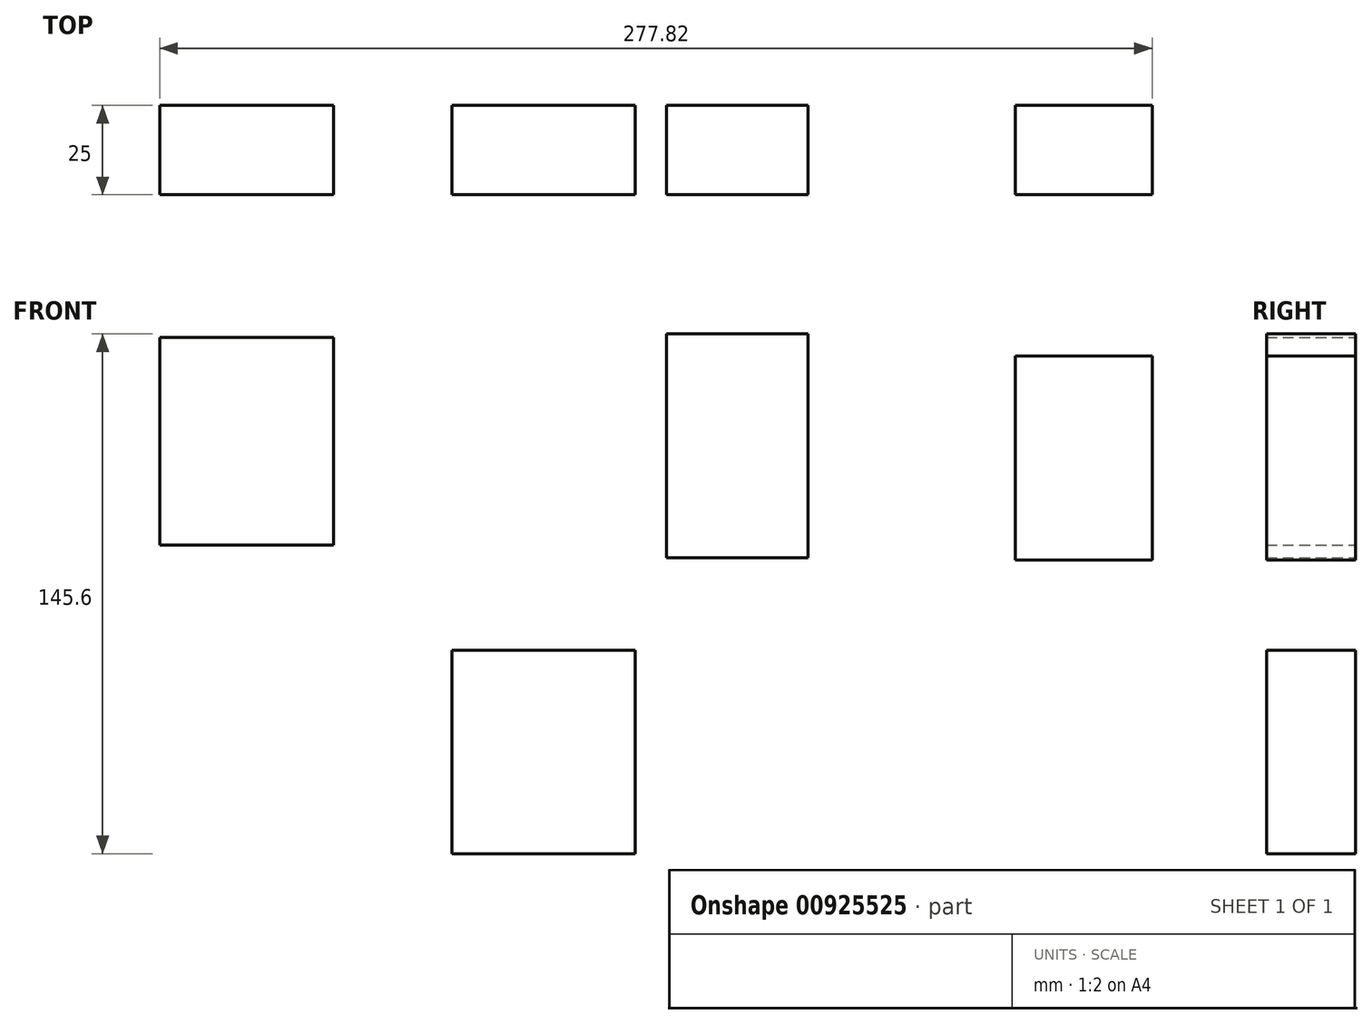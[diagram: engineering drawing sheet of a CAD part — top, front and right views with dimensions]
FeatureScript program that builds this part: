
annotation { "Feature Type Name" : "Feature", "Feature Type Description" : "" }
export const myFeature = defineFeature(function(context is Context, id is Id, definition is map)
    precondition{}
    {
        {
            var Q0;
            Q0=qCreatedBy(makeId("Front.planeOp"),FACE);
            var sketch = newSketch(context, id + "F0", { "sketchPlane" : qUnion([Q0])});
            skLineSegment(sketch, "E0.bottom", {"start": v(-145.24, 17.95) * mm, "end": v(-96.56, 17.95) * mm});
            skLineSegment(sketch, "E0.top", {"start": v(-145.24, 76.15) * mm, "end": v(-96.56, 76.15) * mm});
            skLineSegment(sketch, "E0.left", {"start": v(-145.24, 17.95) * mm, "end": v(-145.24, 76.15) * mm});
            skLineSegment(sketch, "E0.right", {"start": v(-96.56, 17.95) * mm, "end": v(-96.56, 76.15) * mm});
            skPoint(sketch, "E0.middle", {"position": v(-120.9, 47.05) * mm});
            skLineSegment(sketch, "E1.bottom", {"start": v(-3.4, 14.43) * mm, "end": v(36.19, 14.43) * mm});
            skLineSegment(sketch, "E1.top", {"start": v(-3.4, 77.14) * mm, "end": v(36.19, 77.14) * mm});
            skLineSegment(sketch, "E1.left", {"start": v(-3.4, 14.43) * mm, "end": v(-3.4, 77.14) * mm});
            skLineSegment(sketch, "E1.right", {"start": v(36.19, 14.43) * mm, "end": v(36.19, 77.14) * mm});
            skPoint(sketch, "E1.middle", {"position": v(16.4, 45.79) * mm});
            skLineSegment(sketch, "E2.bottom", {"start": v(94.28, 13.75) * mm, "end": v(132.58, 13.75) * mm});
            skLineSegment(sketch, "E2.top", {"start": v(94.28, 70.9) * mm, "end": v(132.58, 70.9) * mm});
            skLineSegment(sketch, "E2.left", {"start": v(94.28, 13.75) * mm, "end": v(94.28, 70.9) * mm});
            skLineSegment(sketch, "E2.right", {"start": v(132.58, 13.75) * mm, "end": v(132.58, 70.9) * mm});
            skPoint(sketch, "E2.middle", {"position": v(113.43, 42.32) * mm});
            skLineSegment(sketch, "E3.bottom", {"start": v(-63.45, -68.46) * mm, "end": v(-12.17, -68.46) * mm});
            skLineSegment(sketch, "E3.top", {"start": v(-63.45, -11.47) * mm, "end": v(-12.17, -11.47) * mm});
            skLineSegment(sketch, "E3.left", {"start": v(-63.45, -68.46) * mm, "end": v(-63.45, -11.47) * mm});
            skLineSegment(sketch, "E3.right", {"start": v(-12.17, -68.46) * mm, "end": v(-12.17, -11.47) * mm});
            skPoint(sketch, "E3.middle", {"position": v(-37.81, -39.96) * mm});
            skSolve(sketch);
        }
        {
            var Q0;
            Q0 = qSketchRegion(id + "F0", true);
            extrude(context, id + "F1", {"entities" : qUnion([Q0]), "depth" : 25 * mm, "offsetDistance" : 25 * mm});
        }
    });
